# Revit family: Building-SurfaceMountingEnclosures-GEWISS-44CEP-PANELS_DIN_1X
name_source: partatom
category: Apparecchi elettrici
revit_build: Autodesk Revit 2016 (Build: 20161004_0715(x64)
units: mm (PartAtom-declared; Revit-internal decimal feet)

## family parameters
Basato su piano di lavoro = Sì
Condiviso = No
Mantenere orientamento annotazione = No
Numero OmniClass = 23.80.30.11.17
Punto di calcolo locali = Sì
Quota connettore circolare = Usa diametro
Sempre verticale = No
Taglio con vuoti quando caricato = No
Tipo di parte = Normale
Titolo OmniClass = Distribution Boards and Control Panels

## types (2) — shared parameters
Altezza = 356 mm  [stored 1.16798 ft]
Catalogue = BUILDING
Catalogue Range = 44 CEP
Characteristics = Halogen free
Colour = Grey RAL 7035
Cornice = GEWISS - GRIGIO
Electrocod = 1310
For boards = 44 CEP
GEWISS SCHEDA TECNICA = http://pro.gewiss.com
H_da terra = 547 mm
IDF = c9947e56-91a3-46b9-b48b-44b334458f86
IDT = 6b5b4bd3-b3c6-410c-8e2b-0edb16ce71f3
Immagine tipo = GW44852.jpg
Larghezza foro = 252 mm  [stored 0.826772 ft]
Lunghezza = 276 mm  [stored 0.905512 ft]
Pannello = GEWISS - GRIGIO RAL 7035
Produttore = GEWISS S.p.A.
Prospetto di default = 1219 mm
SEO = Panel
Spessore = 5 mm  [stored 0.0164042 ft]
Technical sheet = https://www.gewiss.com
Type of material = Halogen free secondo norma EN 50267-2-2
URL = https://www.gewiss.com
Version file RFA = 18.0
Voltaggio = NP
Watt = NP

## per-type parameters (varying)
| type | Descrizione | EAN code | For boards LxH (mm) | Modello | No. of modules EN 50022 | No. of modules EN 50022: | Suitable for |
| GW44853 - COVER PANEL WITH WINDOW 14M.CEP 316X396 | COVER PANEL WITH WINDOW 14M.CEP 316X396 | 8011564111349 | 316x396 | GW44853 | 14 | 14 | Moulded case max 160 A |
| GW44852 - COVER PANEL WITH WINDOW 8M.CEP 236X316 | COVER PANEL WITH WINDOW 8M.CEP 236X316 | 8011564111332 | 236x316 | GW44852 | 8 | 8 | Moulded case max 125 A |

note: [stored X ft] marks values corroborated as IEEE doubles in the binary element streams (Revit-internal decimal feet)

## geometry (parser evidence)
native form markers: Blend x2
no freeform markers — native parametric forms only
